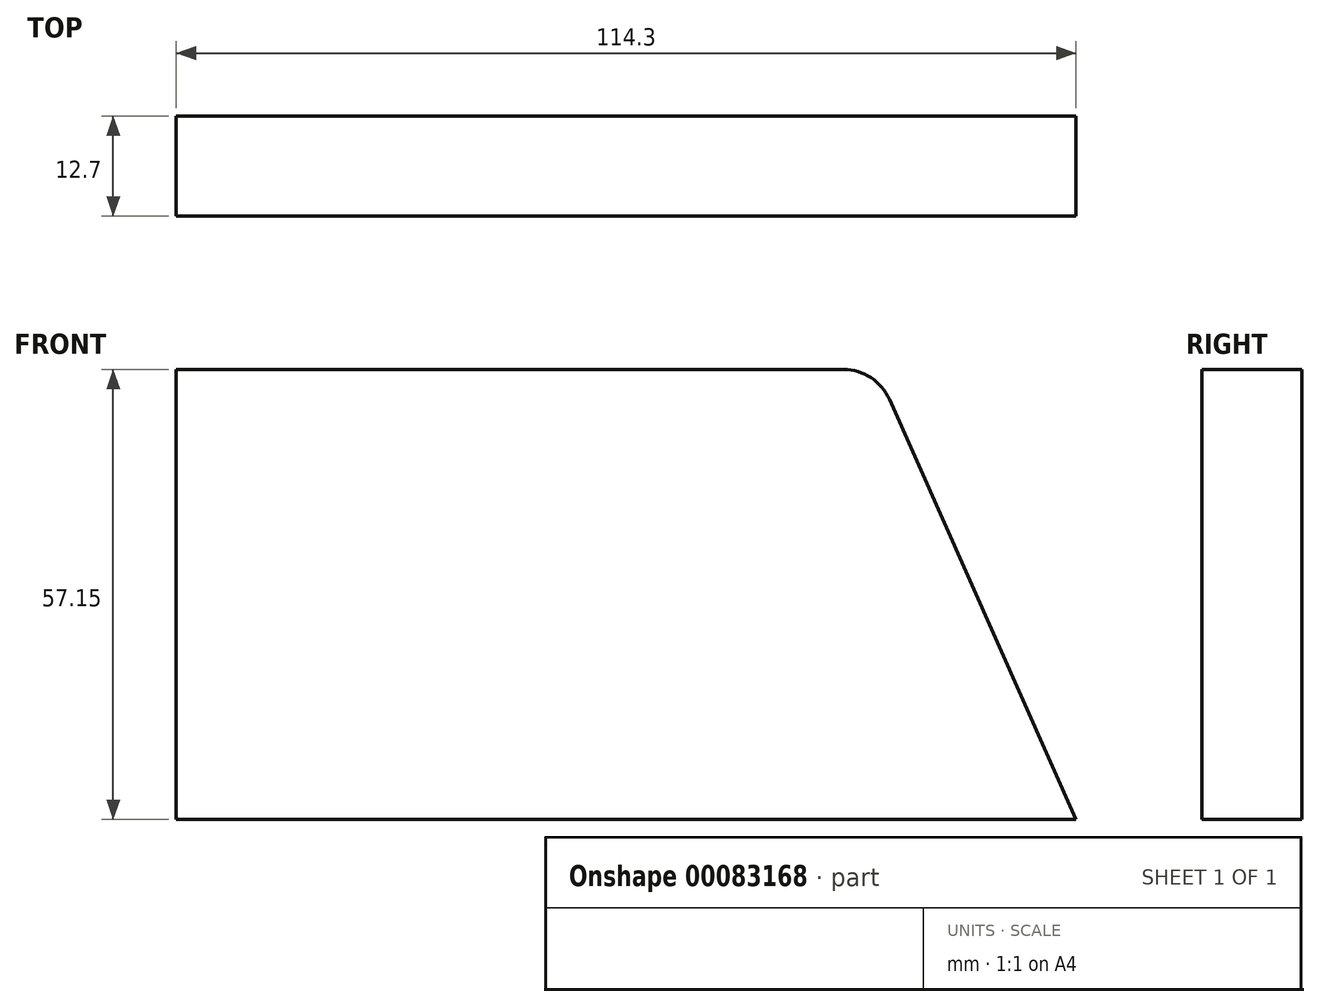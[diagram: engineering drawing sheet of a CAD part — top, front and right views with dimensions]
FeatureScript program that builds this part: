
annotation { "Feature Type Name" : "Feature", "Feature Type Description" : "" }
export const myFeature = defineFeature(function(context is Context, id is Id, definition is map)
    precondition{}
    {
        {
            var Q0;
            Q0=qCreatedBy(makeId("Front.planeOp"),FACE);
            var sketch = newSketch(context, id + "F0", { "sketchPlane" : qUnion([Q0])});
            skLineSegment(sketch, "E0.bottom", {"start": v(114.3, 0) * mm, "end": v(0, 0) * mm});
            skLineSegment(sketch, "E0.top", {"start": v(84.77, 57.15) * mm, "end": v(0, 57.15) * mm});
            skLineSegment(sketch, "E0.left", {"start": v(114.3, 0) * mm, "end": v(114.3, 0) * mm});
            skLineSegment(sketch, "E0.right", {"start": v(0, 0) * mm, "end": v(0, 57.15) * mm});
            skLineSegment(sketch, "E1", {"start": v(90.58, 53.38) * mm, "end": v(114.3, 0) * mm});
            skPoint(sketch, "E2.visualSharp", {"position": v(88.9, 57.15) * mm});
            skArc(sketch, "E2.filletArc", {"start": v(90.58, 53.38) * mm, "mid": v(88.23, 56.12) * mm, "end": v(84.77, 57.15) * mm});
            skSolve(sketch);
        }
        {
            var Q0;
            Q0=makeQuery(id+"F0.imprint","IMPRINT",FACE,{"disambiguationData":[TD([[makeQuery(id+"F0.imprint","IMPRINT",EDGE,{"derivedFrom":sQuery(id+"F0.wireOp",EDGE,"E0.bottom")}),-1.0]])]});
            extrude(context, id + "F1", {"entities" : qUnion([Q0]), "oppositeDirection" : true, "depth" : 12.7 * mm});
        }
    });
